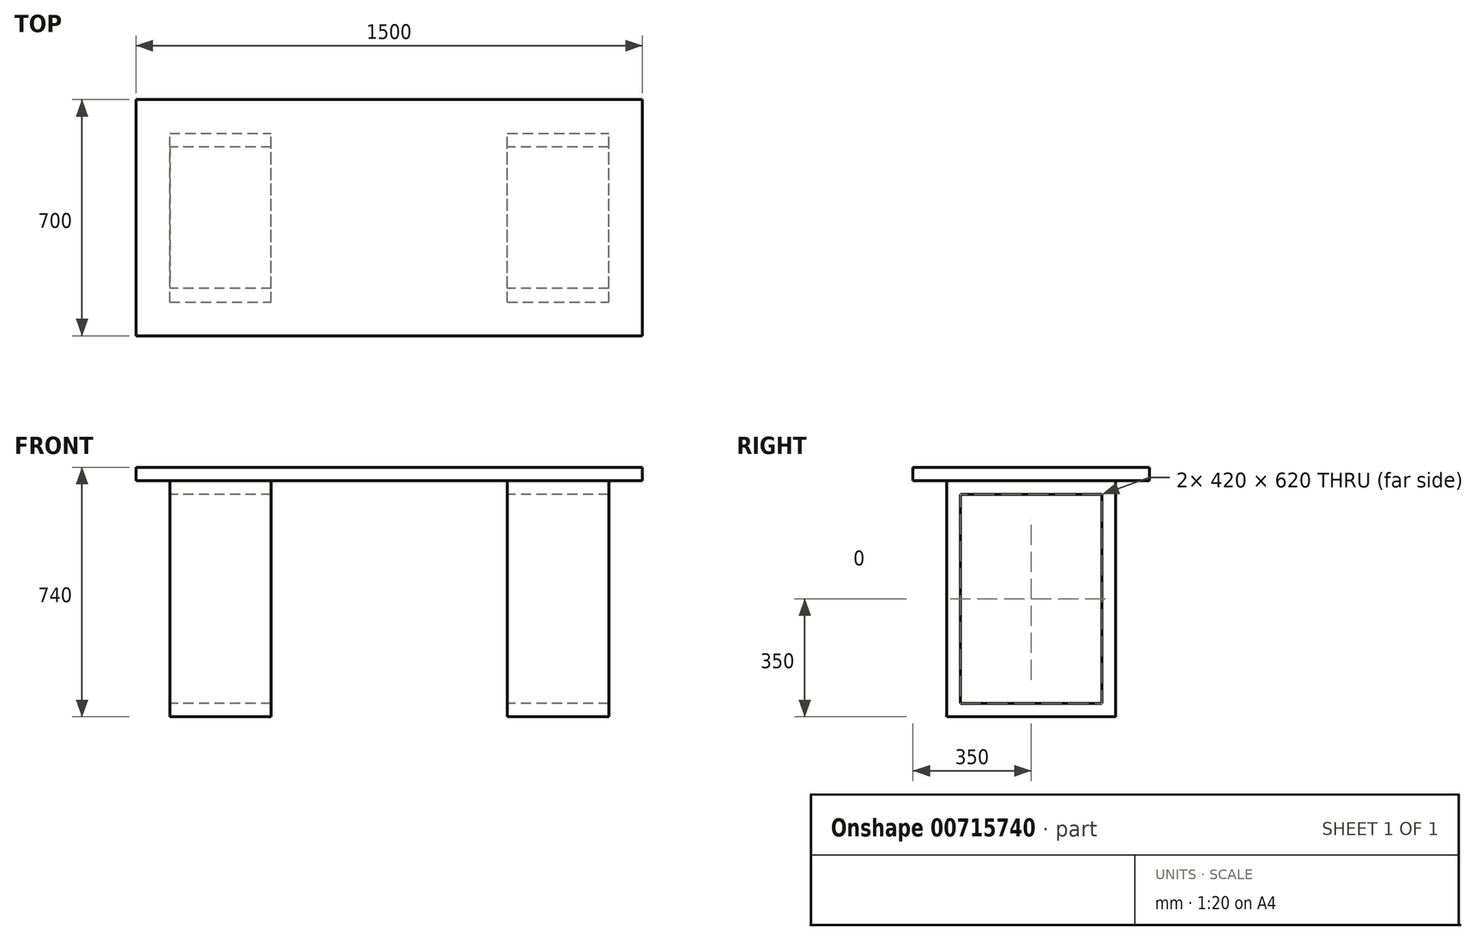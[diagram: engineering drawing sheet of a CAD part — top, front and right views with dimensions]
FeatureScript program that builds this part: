
annotation { "Feature Type Name" : "Feature", "Feature Type Description" : "" }
export const myFeature = defineFeature(function(context is Context, id is Id, definition is map)
    precondition{}
    {
        {
            var Q0;
            Q0=qCreatedBy(makeId("Top.planeOp"),FACE);
            var sketch = newSketch(context, id + "F0", { "sketchPlane" : qUnion([Q0])});
            skLineSegment(sketch, "E0.bottom", {"start": v(0, 0) * mm, "end": v(1500, 0) * mm});
            skLineSegment(sketch, "E0.top", {"start": v(0, -700) * mm, "end": v(1500, -700) * mm});
            skLineSegment(sketch, "E0.left", {"start": v(0, 0) * mm, "end": v(0, -700) * mm});
            skLineSegment(sketch, "E0.right", {"start": v(1500, 0) * mm, "end": v(1500, -700) * mm});
            skSolve(sketch);
        }
        {
            var Q0;
            Q0=makeQuery(id+"F0.imprint","IMPRINT",FACE,{"disambiguationData":[TD([[makeQuery(id+"F0.imprint","IMPRINT",EDGE,{"derivedFrom":sQuery(id+"F0.wireOp",EDGE,"E0.bottom")}),-1.0]])]});
            extrude(context, id + "F1", {"entities" : qUnion([Q0]), "oppositeDirection" : true, "depth" : 40 * mm, "offsetDistance" : 25 * mm});
        }
        {
            var Q0;
            Q0=makeQuery(id+"F1.opExtrude","CAP_FACE",FACE,{"disambiguationData":[OSD([sQuery(id+"F0.wireOp",EDGE,"E0.bottom"),sQuery(id+"F0.wireOp",EDGE,"E0.top"),sQuery(id+"F0.wireOp",EDGE,"E0.left"),sQuery(id+"F0.wireOp",EDGE,"E0.right")])],"isStart":false});
            var sketch = newSketch(context, id + "F2", { "sketchPlane" : qUnion([Q0])});
            skLineSegment(sketch, "E1.bottom", {"start": v(100, 600) * mm, "end": v(400, 600) * mm});
            skLineSegment(sketch, "E1.top", {"start": v(100, 100) * mm, "end": v(400, 100) * mm});
            skLineSegment(sketch, "E1.left", {"start": v(100, 600) * mm, "end": v(100, 100) * mm});
            skLineSegment(sketch, "E1.right", {"start": v(400, 600) * mm, "end": v(400, 100) * mm});
            skLineSegment(sketch, "E2.bottom", {"start": v(1100, 600) * mm, "end": v(1400, 600) * mm});
            skLineSegment(sketch, "E2.top", {"start": v(1100, 100) * mm, "end": v(1400, 100) * mm});
            skLineSegment(sketch, "E2.left", {"start": v(1100, 600) * mm, "end": v(1100, 100) * mm});
            skLineSegment(sketch, "E2.right", {"start": v(1400, 600) * mm, "end": v(1400, 100) * mm});
            skSolve(sketch);
        }
        {
            var Q0;
            Q0 = qSketchRegion(id + "F2", true);
            extrude(context, id + "F3", {"entities" : qUnion([Q0]), "operationType" : NewBodyOperationType.ADD, "depth" : 700 * mm, "offsetDistance" : 25 * mm});
        }
        {
            var Q0;
            Q0=makeQuery(id+"F3.opExtrude","SWEPT_FACE",FACE,{"disambiguationData":[OSD([sQuery(id+"F2.wireOp",EDGE,"E1.left")])]});
            var sketch = newSketch(context, id + "F4", { "sketchPlane" : qUnion([Q0])});
            skLineSegment(sketch, "E3.bottom", {"start": v(140, -80) * mm, "end": v(560, -80) * mm});
            skLineSegment(sketch, "E3.top", {"start": v(140, -700) * mm, "end": v(560, -700) * mm});
            skLineSegment(sketch, "E3.left", {"start": v(140, -80) * mm, "end": v(140, -700) * mm});
            skLineSegment(sketch, "E3.right", {"start": v(560, -80) * mm, "end": v(560, -700) * mm});
            skSolve(sketch);
        }
        {
            var Q0;
            Q0 = qSketchRegion(id + "F4", true);
            extrude(context, id + "F5", {"entities" : qUnion([Q0]), "operationType" : NewBodyOperationType.REMOVE, "oppositeDirection" : true, "depth" : 1328 * mm, "offsetDistance" : 25 * mm});
        }
    });
